# Revit family: Deca_Ducha higiênica com registro e derivação_DK_1984.16.ACT
name_source: partatom
category: Plumbing Fixtures
units: mm (PartAtom-declared; Revit-internal decimal feet)

## family parameters
Cut with Voids When Loaded = No
Host = Face
Part Type = Normal
Room Calculation Point = No
Round Connector Dimension = Use Radius
Shared = No

## types (1)
- 1984.GL16.ACT.RD_Red Gold
    Acompanha o Produto = Acompanha Parafuso e bucha para fixação
    Aprovado por = quattroD
    Atendimento ao Cliente = 0800-0117073
    Categoria = METAIS PARA BANHEIRO
    Composição Anel Vedação = -
    Composição Assento = -
    Composição Básica = Liga cobre (bronze e latão),Aço,Plástico de Engenharia,Elastômeros
    Composição Componente = -
    Consumo = -
    Cor Interna = -
    Cor Principal = Red Gold
    Cor Secundária = Branco
    Cores Componente = -
    Criado por = quattroD
    Código Pai = 1984.16.ACT
    Default Elevation = 0.7 m
    Description = Ducha higiênica com registro e derivação
    Diâmetro Água Fria = 0.02 m
    Informações Complementares = -
    Itens de Instalação = -
    Linha = DK
    Manufacturer = Deca
    Material = Deca_Red Gold
    Material Secundário = Deca_Plástico - Branco
    Model = 1984.GL16.ACT.RD
    Norma = NBR14877
    Peso Líquido (Kg) = 0.921
    Pressão máx. funcionamento = 40 MCA
    Pressão mín. Aquec. Acúmulo = -
    Pressão mín. Aquec. Passagem = -
    Pressão mín. funcionamento = 2 MCA
    Raio Água Fria = 0.01 m
    Saída de Esgoto = -
    Segmento = Banheiro Luxo
    Tipo de dispositivo economizador = Não
    Tipo de mecanismo utilizado = MVC -1/4 volta
    Tipo de rosca de entrada = BSP NBR 8133
    Tipo de rosca de saída = -
    URL = www.deca.com.br
    Vazão na Pressão máx. (L/min) = 15
    Vazão na Pressão mín. (L/min) = 5

note: source unit labels omitted for Vazão na Pressão máx. (L/min), Vazão na Pressão mín. (L/min) — the stored unit's dimension contradicts the parameter name (converter mislabeling)

## geometry (parser evidence)
native form markers: Sweep x1
no freeform markers — native parametric forms only
